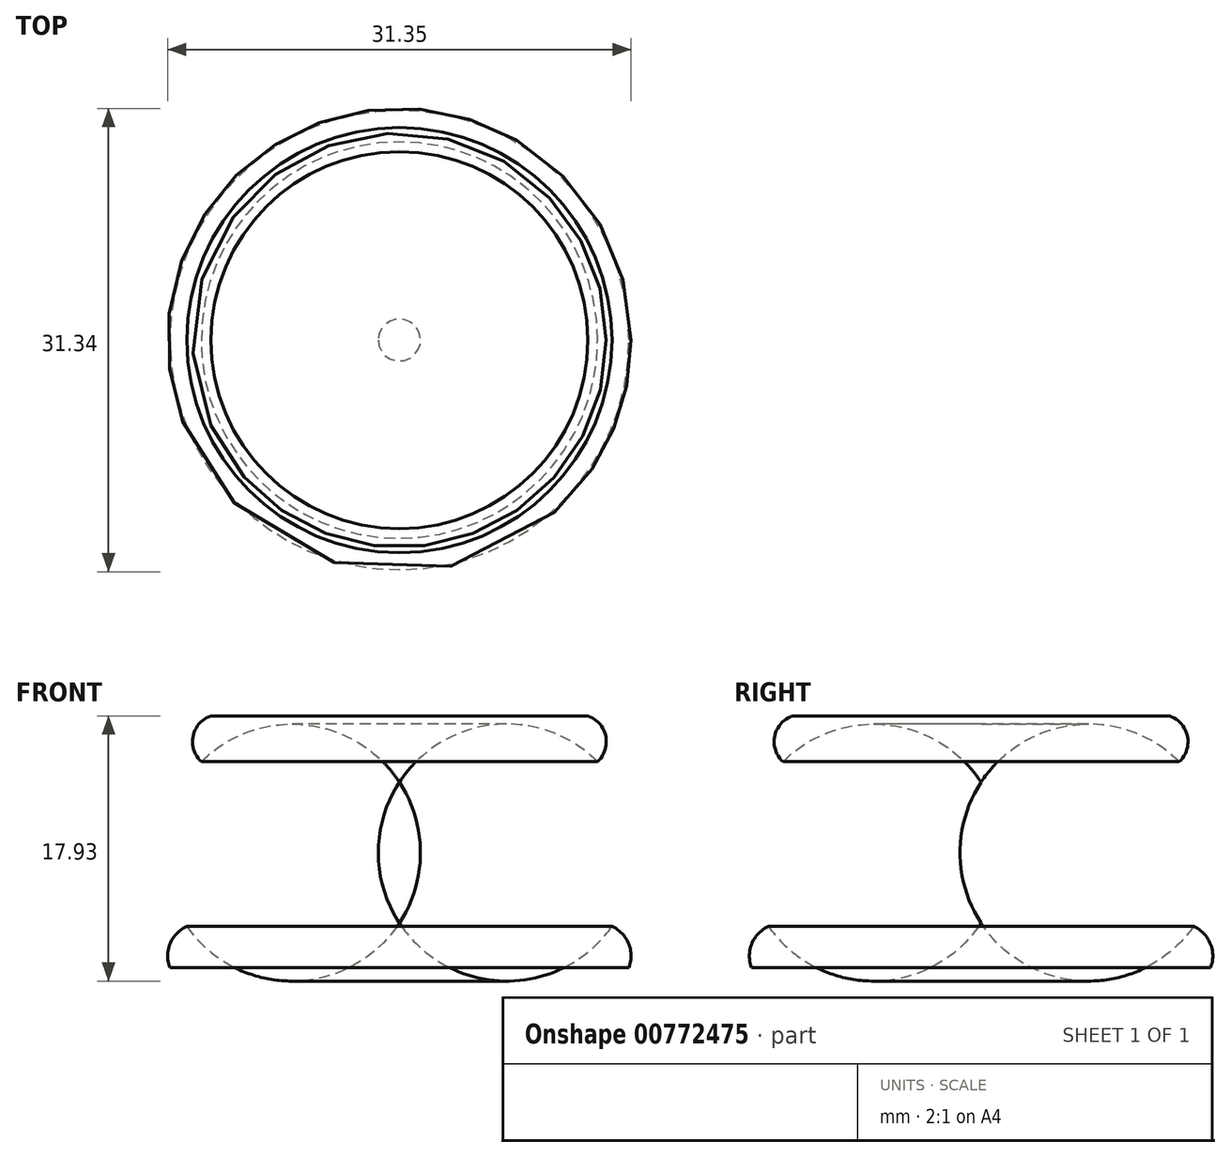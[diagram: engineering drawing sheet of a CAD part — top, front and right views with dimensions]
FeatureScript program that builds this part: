
annotation { "Feature Type Name" : "Feature", "Feature Type Description" : "" }
export const myFeature = defineFeature(function(context is Context, id is Id, definition is map)
    precondition{}
    {
        {
            var Q0;
            Q0=qCreatedBy(makeId("Front.planeOp"),FACE);
            var sketch = newSketch(context, id + "F0", { "sketchPlane" : qUnion([Q0])});
            skArc(sketch, "E0", {"start": v(8.33, 17.01) * mm, "mid": v(7.13, 15.65) * mm, "end": v(7.68, 13.92) * mm});
            skArc(sketch, "E1", {"start": v(7.68, 13.92) * mm, "mid": v(5.16, 8.53) * mm, "end": v(6.7, 2.78) * mm});
            skArc(sketch, "E2", {"start": v(6.7, 2.78) * mm, "mid": v(5.57, 1.62) * mm, "end": v(5.55, 0) * mm});
            skLineSegment(sketch, "E3", {"start": v(5.55, 0) * mm, "end": v(17.2, 0) * mm});
            skLineSegment(sketch, "E4", {"start": v(17.2, 17) * mm, "end": v(8.33, 17.01) * mm});
            skLineSegment(sketch, "E5", {"start": v(17.2, 17) * mm, "end": v(18.46, 17) * mm});
            skLineSegment(sketch, "E6", {"start": v(18.46, 0) * mm, "end": v(17.2, 0) * mm});
            skPoint(sketch, "E7.end.orphan", {"position": v(17.2, 1.48) * mm});
            skPoint(sketch, "E8.start.orphan", {"position": v(27.32, 17) * mm});
            skPoint(sketch, "E9.orphan", {"position": v(27.32, 0) * mm});
            skPoint(sketch, "E10.start.orphan", {"position": v(22.26, 17) * mm});
            skPoint(sketch, "E11.orphan", {"position": v(22.26, 0) * mm});
            skPoint(sketch, "E12.start.orphan", {"position": v(19.72, 17) * mm});
            skPoint(sketch, "E13.orphan", {"position": v(19.72, 0) * mm});
            skLineSegment(sketch, "E14", {"start": v(18.46, 17) * mm, "end": v(21.08, 17) * mm});
            skLineSegment(sketch, "E15", {"start": v(21.08, 17) * mm, "end": v(21.08, 0) * mm});
            skLineSegment(sketch, "E16", {"start": v(21.08, 0) * mm, "end": v(18.46, 0) * mm});
            skSolve(sketch);
        }
        {
            var Q0;
            Q0 = qSketchRegion(id + "F0", true);
            var Q1;
            Q1=sQuery(id+"F0.wireOp",EDGE,"E15");
            revolve(context, id + "F1", {"surfaceOperationType" : NewSurfaceOperationType.NEW, "entities" : qUnion([Q0]), "axis" : qUnion([Q1]), "revolveType" : RevolveType.FULL});
        }
    });
